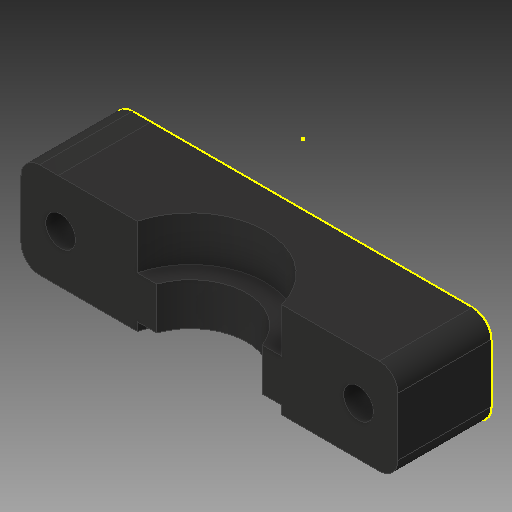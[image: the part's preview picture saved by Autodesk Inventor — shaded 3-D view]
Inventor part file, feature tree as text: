
AUTODESK INVENTOR PART (.ipt)
format: ipt  version: 2018 (Build 220112000, 112)  size: 148,480 bytes
history: native  units: mm
features: sketch x5, other x3
ambient origin geometry x8: Origin, YZ Plane, XZ Plane, XY Plane, X Axis, Y Axis, Z Axis, Center Point
bodies: Solid1 (feature_tree)
feature tree (8):
  other  "Hotend Clamp P1_MIR.ipt"
  other  "Solid1::Hotend Clamp P1_MIR.ipt"
  other  "TaggingFeature1"
  sketch  "Sketch1"  dims[d0=10.0mm]
  sketch  "Sketch2"
  sketch  "Sketch3"
  sketch  "Sketch4"
  sketch  "Sketch5"
